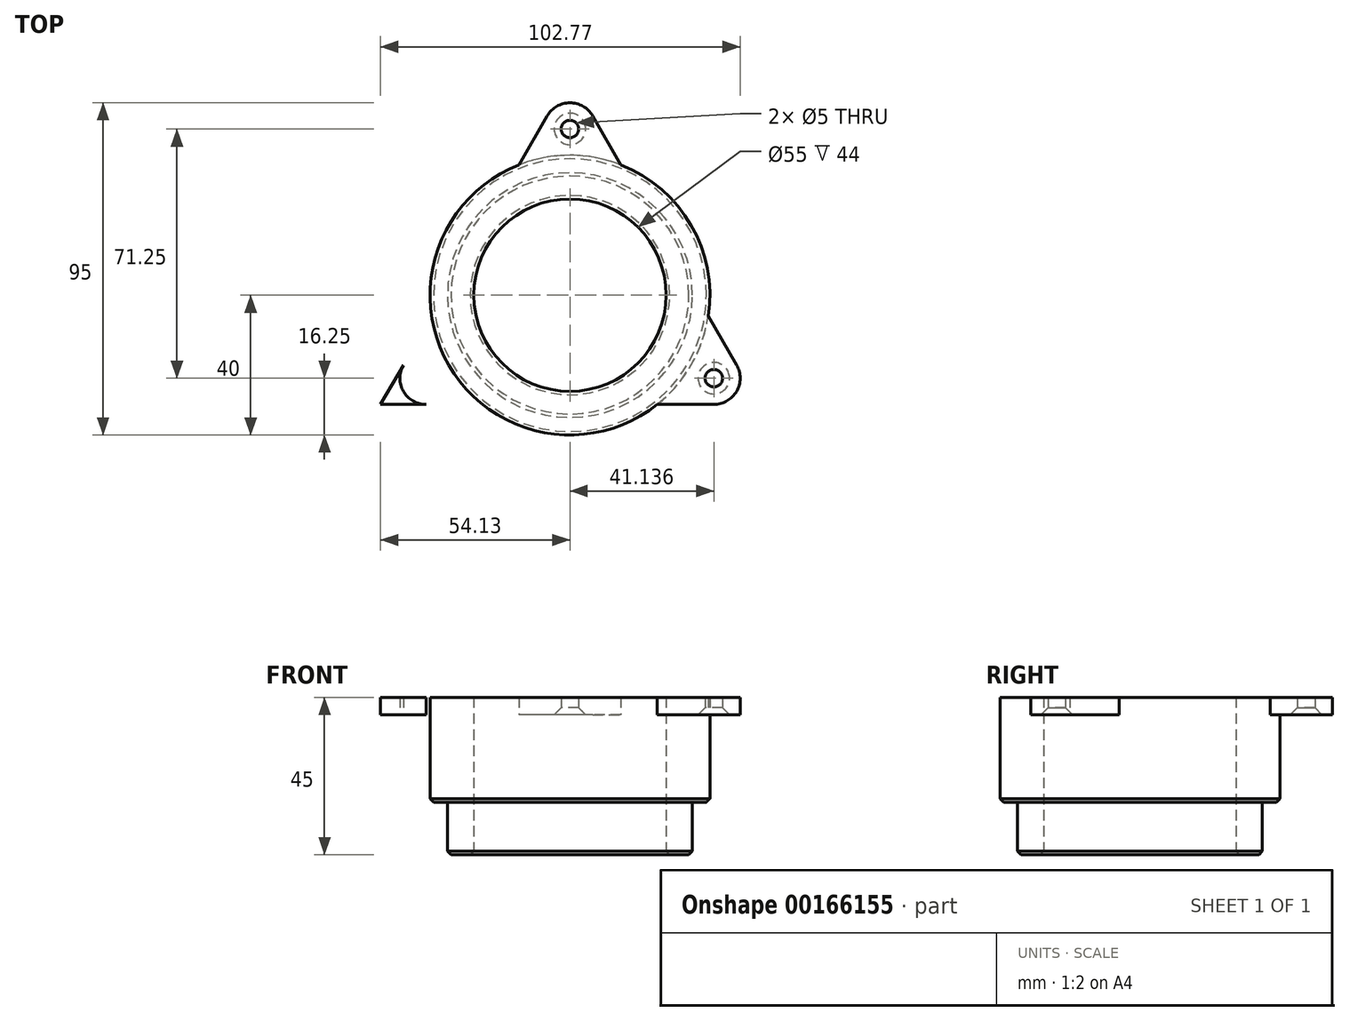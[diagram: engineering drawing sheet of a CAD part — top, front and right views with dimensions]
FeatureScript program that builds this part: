
annotation { "Feature Type Name" : "Feature", "Feature Type Description" : "" }
export const myFeature = defineFeature(function(context is Context, id is Id, definition is map)
    precondition{}
    {
        {
            var Q0;
            Q0=qCreatedBy(makeId("Top.planeOp"),FACE);
            var sketch = newSketch(context, id + "F0", { "sketchPlane" : qUnion([Q0])});
            skCircle(sketch, "E0", {"center": v(0, 0) * mm, "radius": 40 * mm});
            skArc(sketch, "E1", {"start": v(6.5, 51.25) * mm, "mid": v(0, 55) * mm, "end": v(-6.5, 51.25) * mm});
            skLineSegment(sketch, "E2", {"start": v(6.5, 51.25) * mm, "end": v(14.58, 37.25) * mm});
            skLineSegment(sketch, "E3.MirrorCS", {"start": v(-6.5, 51.25) * mm, "end": v(-14.58, 37.25) * mm});
            skCircle(sketch, "E4", {"center": v(0, 47.5) * mm, "radius": 2.5 * mm});
            skLineSegment(sketch, "E5.1.0", {"start": v(-54.13, -31.25) * mm, "end": v(-39.55, -6) * mm});
            skLineSegment(sketch, "E5.1.1", {"start": v(-54.13, -31.25) * mm, "end": v(-24.97, -31.25) * mm});
            skArc(sketch, "E5.1.2", {"start": v(-47.63, -20) * mm, "mid": v(-47.63, -27.5) * mm, "end": v(-41.14, -31.25) * mm});
            skCircle(sketch, "E5.1.3", {"center": v(-41.14, -23.75) * mm, "radius": 2.5 * mm});
            skLineSegment(sketch, "E5.2.0", {"start": v(41.14, -31.25) * mm, "end": v(24.97, -31.25) * mm});
            skLineSegment(sketch, "E5.2.1", {"start": v(47.63, -20) * mm, "end": v(39.55, -6) * mm});
            skArc(sketch, "E5.2.2", {"start": v(41.14, -31.25) * mm, "mid": v(47.63, -27.5) * mm, "end": v(47.63, -20) * mm});
            skCircle(sketch, "E5.2.3", {"center": v(41.14, -23.75) * mm, "radius": 2.5 * mm});
            skCircle(sketch, "E6", {"center": v(0, 0) * mm, "radius": 27.5 * mm});
            skCircle(sketch, "E7", {"center": v(0, 0) * mm, "radius": 55 * mm, "construction": true});
            skSolve(sketch);
        }
        {
            var Q0;
            Q0=makeQuery(id+"F0.imprint","IMPRINT",FACE,{"disambiguationData":[TD([[makeQuery(id+"F0.imprint","IMPRINT",EDGE,{"derivedFrom":sQuery(id+"F0.wireOp",EDGE,"E6")}),-1.0]])]});
            var Q1;
            {var subQ1=sQuery(id+"F0.wireOp",EDGE,"E5.1.0");Q1=makeQuery(id+"F0.imprint","IMPRINT",FACE,{"disambiguationData":[TD([[makeQuery(id+"F0.imprint","IMPRINT",EDGE,{"derivedFrom":subQ1}),-1.0]])]});}
            var Q2;
            Q2=makeQuery(id+"F0.imprint","IMPRINT",FACE,{"disambiguationData":[TD([[makeQuery(id+"F0.imprint","IMPRINT",EDGE,{"derivedFrom":sQuery(id+"F0.wireOp",EDGE,"E1")}),1.0]])]});
            var Q3;
            {var subQ1=sQuery(id+"F0.wireOp",EDGE,"E5.2.0");Q3=makeQuery(id+"F0.imprint","IMPRINT",FACE,{"disambiguationData":[TD([[makeQuery(id+"F0.imprint","IMPRINT",EDGE,{"derivedFrom":subQ1}),-1.0]])]});}
            extrude(context, id + "F1", {"entities" : qUnion([Q0, Q1, Q2, Q3]), "depth" : 5 * mm});
        }
        {
            var Q0;
            Q0=makeQuery(id+"F0.imprint","IMPRINT",FACE,{"disambiguationData":[TD([[makeQuery(id+"F0.imprint","IMPRINT",EDGE,{"derivedFrom":sQuery(id+"F0.wireOp",EDGE,"E6")}),-1.0]])]});
            extrude(context, id + "F2", {"entities" : qUnion([Q0]), "operationType" : NewBodyOperationType.ADD, "oppositeDirection" : true, "depth" : 25 * mm});
        }
        {
            var Q0;
            Q0=makeQuery(id+"F2.opExtrude","CAP_FACE",FACE,{"disambiguationData":[OSD([sQuery(id+"F0.wireOp",EDGE,"E0"),sQuery(id+"F0.wireOp",EDGE,"E6")])],"isStart":false});
            var sketch = newSketch(context, id + "F3", { "sketchPlane" : qUnion([Q0])});
            skCircle(sketch, "E8", {"center": v(0, 0) * mm, "radius": 35 * mm});
            skSolve(sketch);
        }
        {
            var Q0;
            Q0=makeQuery(id+"F3.imprint","IMPRINT",FACE,{"disambiguationData":[TD([[makeQuery(id+"F3.imprint","IMPRINT",EDGE,{"derivedFrom":sQuery(id+"F3.wireOp",EDGE,"E8")}),1.0]])]});
            extrude(context, id + "F4", {"entities" : qUnion([Q0]), "operationType" : NewBodyOperationType.ADD, "depth" : 15 * mm});
        }
        {
            var Q0;
            Q0=makeQuery(id+"F1.opExtrude","CAP_EDGE",EDGE,{"disambiguationData":[OSD([sQuery(id+"F0.wireOp",EDGE,"E5.1.3")])],"isStart":true});
            var Q1;
            Q1=makeQuery(id+"F1.opExtrude","CAP_EDGE",EDGE,{"disambiguationData":[OSD([sQuery(id+"F0.wireOp",EDGE,"E4")])],"isStart":true});
            var Q2;
            Q2=makeQuery(id+"F1.opExtrude","CAP_EDGE",EDGE,{"disambiguationData":[OSD([sQuery(id+"F0.wireOp",EDGE,"E5.2.3")])],"isStart":true});
            chamfer(context, id + "F5", {"entities" : qUnion([Q0, Q1, Q2]), "width" : 2 * mm, "tangentPropagation" : true});
        }
        {
            var Q0;
            Q0=makeQuery(id+"F2.opExtrude","CAP_EDGE",EDGE,{"disambiguationData":[OSD([sQuery(id+"F0.wireOp",EDGE,"E0")])],"isStart":false});
            var Q1;
            Q1=makeQuery(id+"F4.opExtrude","CAP_EDGE",EDGE,{"disambiguationData":[OSD([sQuery(id+"F3.wireOp",EDGE,"E8")])],"isStart":false});
            var Q2;
            Q2=makeQuery(id+"F4.opExtrude","CAP_EDGE",EDGE,{"disambiguationData":[OSD([sQuery(id+"F0.wireOp",EDGE,"E6")])],"isStart":false});
            chamfer(context, id + "F6", {"entities" : qUnion([Q0, Q1, Q2]), "width" : 1 * mm, "tangentPropagation" : true});
        }
    });
